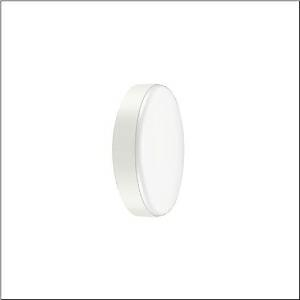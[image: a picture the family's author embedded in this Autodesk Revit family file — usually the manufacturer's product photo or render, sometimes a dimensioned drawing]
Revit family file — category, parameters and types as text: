
# Revit family: round_31_51wc10da42as
name_source: partatom
category: Lighting Fixtures
units: mm (PartAtom-declared; Revit-internal decimal feet)

## family parameters
Cut with Voids When Loaded = No
Host = Face
Light Source = No
Part Type = Normal
Room Calculation Point = No
Round Connector Dimension = Use Diameter
Shared = No

## types (1)
- Round 31 (1 x LED, 2550 lm, 20.5 W, 4000K)
    Apparent Load = 21 VA
    CIE Flux Codes = 44 75 94 94 100
    Color Rendering = 80
    Color Temperature = 4000K
    Default Elevation = 1800 mm
    Description = Round 31, wall and ceiling luminaire, primary optical cover: cover, of PC, opal, light emission: direct distribution, primary light characteristic: symmetric, installation type: surface-mounted, LED, rated luminous flux: 2.550lm, luminous efficacy: 124lm/W, light colour: 840, colour temperature: 4000K, control gear: DALI 2, with terminal, 5-pole, max. 2.5mm², mains connection: 220..240V, AC, 50/60Hz, rated input power: 20.5W, luminaire housing, of PC, traffic white (RAL 9016), diameter: 350mm, brightness and presence sensor, HF sensor, protection rating (complete): IP65, insulation class (complete): insulation class II (safety insulation), certification: CE, impact resistance: IK10, permissible operating ambient temperature: -20..+40°C, permissible storage temperature: -20..+60°C, packaging unit: 1 piece
    Height = 97 mm
    Lamp = 1 x LED
    Lamp Light Flux = 2550 lm
    Lamp Power = 20.5 W
    Lamp count = 1
    Length = 350 mm
    Luminous efficacy = 124 lm/W
    Manufacturer = Siteco
    ModVariant = No
    Model = 51WC10DA42AS
    Mounting Place = Wall
    Mounting Type = Surface mounted
    Number of Poles = 1
    OnlyDefault = Yes
    Power Factor = 1
    Product Name = Round 31
    Product group = wall and ceiling luminaire | wall mounted
    ProductGroupID = 2001
    Protection Class = Protection class II
    Protection Degree = IP 65
    RLX_Detail_Level = 1
    RLX_Emergency_Light_Flux = 0 lm
    RLX_Emergency_Type = 0
    RLX_Emergency_Type_DB = No
    RlxData = <blob elided: 29853 chars, md5=d743a319>
    Socket = socket
    Standby Power = 0 W
    System Light Flux = 2550 lm
    System Power = 21 W
    Type Comments = Product without accessories
    Type Image = l_1007027.jpg
    URL = http://relux.com
    VarID = ---
    Voltage = 0 V
    Weight = 0.00 kg
    Width = 0 mm  [stored 0 ft]

note: [stored X ft] marks values corroborated as IEEE doubles in the binary element streams (Revit-internal decimal feet)

## geometry (parser evidence)
native form markers: Blend x4, Sweep x11
no freeform markers — native parametric forms only
